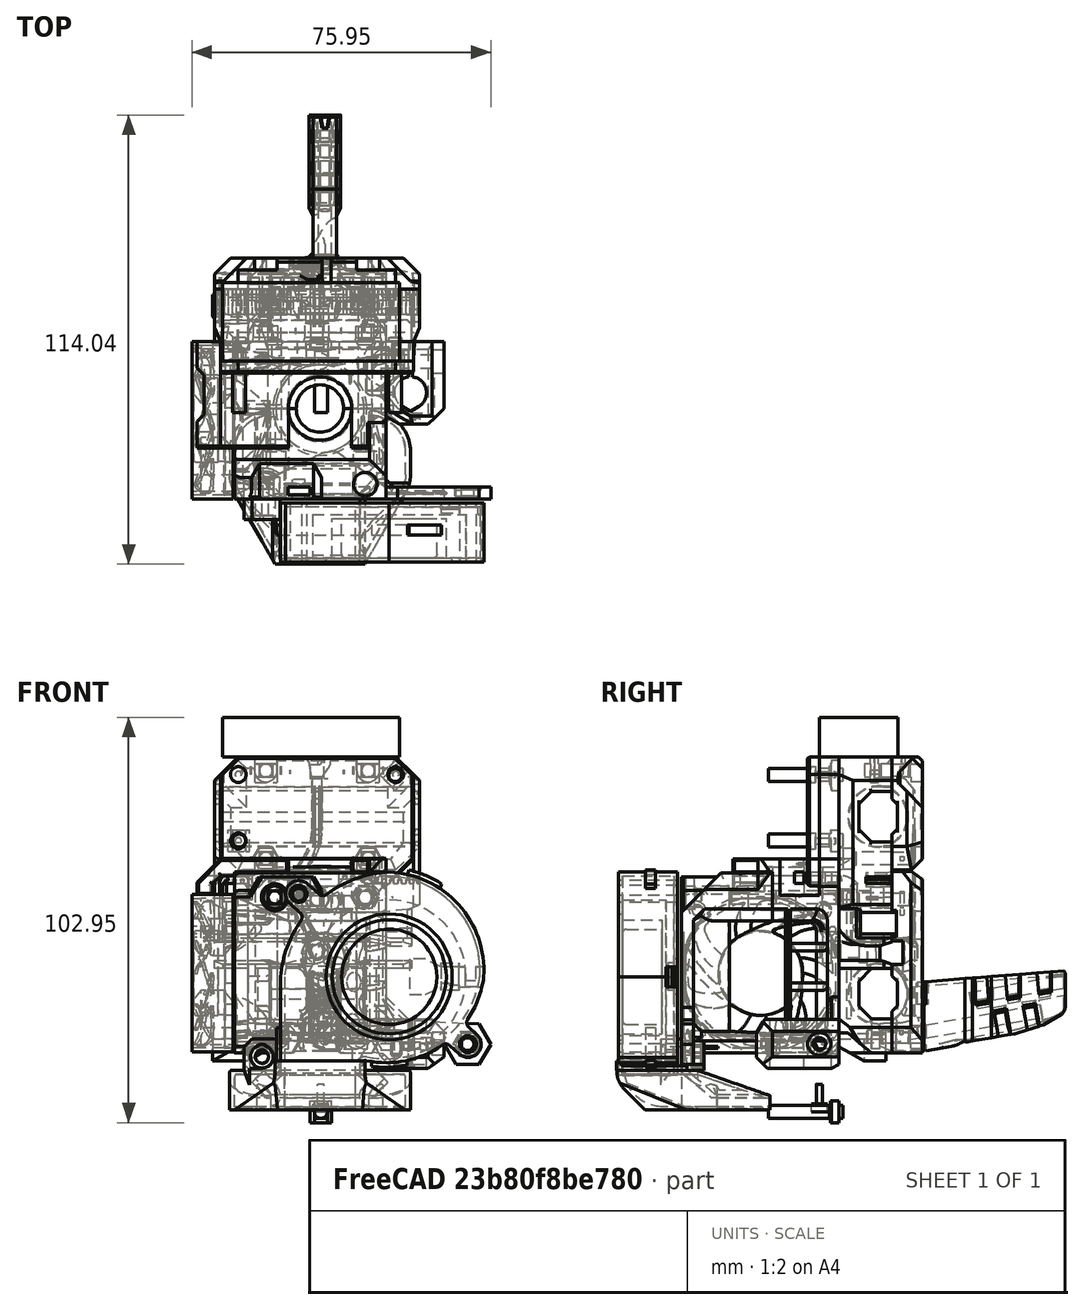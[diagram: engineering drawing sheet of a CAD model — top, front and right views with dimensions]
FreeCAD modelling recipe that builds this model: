
FCSTD DOCUMENT  (FreeCAD 0.18R16146 (Git))
Label: origin
License: All rights reserved
LicenseURL: http://en.wikipedia.org/wiki/All_rights_reserved
objects: Part::Feature×21, Part::Box×21, Part::Cut×14, Part::MultiFuse×7, Part::Chamfer×5, Part::Cylinder×3, Part::Fillet×1
note: 72 computed .brp shape members not serialized (recipe doc carries the construction recipe); baked Part::Feature solids carry a one-line shape summary decoded from their .brp

FEATURE [Part::Feature] Part__Feature005001  label="nozzle_fan_duct001"
  shape: bbox 46 x 38.98 x 18 mm, 128 faces (baked)
FEATURE [Part::Feature] Part__Feature006002  label="x_carriage_back_mk2.5s_v026"
  shape: bbox 52.01 x 8.271 x 75.21 mm, 515 faces, 2 solids (baked)
FEATURE [Part::Feature] Part__Feature003001  label="body001"
  shape: bbox 64.24 x 27.71 x 94.51 mm, 731 faces (baked)
FEATURE [Part::Feature] Part__Feature007001  label="cable_guide_back_a001"
  shape: bbox 9.081 x 19.43 x 18.86 mm, 61 faces (baked)
FEATURE [Part::Feature] Part__Feature008001  label="cable_guide_back_b001"
  shape: bbox 14.17 x 31.38 x 17 mm, 108 faces (baked)
FEATURE [Part::Feature] Part__Feature002001  label="cover001"
  shape: bbox 65.38 x 24.39 x 50.21 mm, 417 faces (baked)
FEATURE [Part::Feature] Part__Feature001001  label="x_carriage001"
  shape: bbox 52.5 x 22.36 x 91 mm, 735 faces (baked)
FEATURE [Part::Box] Box  label="Cube"
  AttacherType = Attacher::AttachEngine3D
  Height = 58
  Length = 78
  Placement = pos=(-37,-32,94) rot=(0,0,1;0rad)
  Width = 65
FEATURE [Part::Box] Box001  label="Cube001"
  AttacherType = Attacher::AttachEngine3D
  Height = 58
  Length = 78
  Placement = pos=(-37,-32,94) rot=(0,0,1;0rad)
  Width = 65
FEATURE [Part::Cut] Cut
  Base = -> Part__Feature001001
  Tool = -> Box001
FEATURE [Part::Cut] Cut001
  Base = -> Part__Feature003001
  Tool = -> Box
FEATURE [Part::Box] Box002  label="Cube002"
  AttacherType = Attacher::AttachEngine3D
  Height = 58
  Length = 78
  Placement = pos=(-37,-32,64.24) rot=(0,0,1;0rad)
  Width = 65
FEATURE [Part::Cut] Cut002
  Base = -> Cut001
  Tool = -> Box002
FEATURE [Part::Box] Box003  label="Cube003"
  AttacherType = Attacher::AttachEngine3D
  Height = 10
  Length = 16.06
  Placement = pos=(-8.26,-22,58) rot=(0,0,1;0rad)
  Width = 19
FEATURE [Part::Feature] Part__Feature046  label="nozzle_fan"
  Placement = pos=(-10.225,-36,34.3) rot=(0,0,1;1.5708rad)
  shape: bbox 52.65 x 15 x 52.12 mm, 76 faces (baked)
FEATURE [Part::Feature] Part__Feature008002  label="cover002"
  shape: bbox 65.38 x 24.39 x 50.21 mm, 417 faces (baked)
FEATURE [Part::Fillet] Fillet
  Base = -> Box003
  Edges = 2 edges r=8: [Edge3,Edge7]
  Placement = pos=(0,-1,0) rot=(0,0,1;0rad)
FEATURE [Part::Cut] Cut003
  Base = -> Cut002
  Tool = -> Fillet
FEATURE [Part::Box] Box004  label="Cube004"
  AttacherType = Attacher::AttachEngine3D
  Height = 1
  Length = 3
  Placement = pos=(6,-6,63.24) rot=(0,0,1;0rad)
  Width = 6
FEATURE [Part::Box] Box005  label="Cube005"
  AttacherType = Attacher::AttachEngine3D
  Height = 2
  Length = 36
  Placement = pos=(-22,-1,62.24) rot=(0,0,1;0rad)
  Width = 6
FEATURE [Part::Box] Box006  label="Cube006"
  AttacherType = Attacher::AttachEngine3D
  Height = 6
  Length = 6
  Placement = pos=(12.32,-24,59.24) rot=(0,0,1;0rad)
  Width = 8.43
FEATURE [Part::Cut] Cut004
  Base = -> Cut003
  Tool = -> Box006
FEATURE [Part::MultiFuse] Fusion
  Shapes = -> [Cut004,Box005,Box004]
FEATURE [Part::Box] Box007  label="Cube007"
  AttacherType = Attacher::AttachEngine3D
  Height = 17
  Length = 17
  Placement = pos=(-35.45,0,90.2) rot=(0,0,1;0rad)
  Width = 21
FEATURE [Part::Box] Box008  label="Cube008"
  AttacherType = Attacher::AttachEngine3D
  Height = 17
  Length = 17
  Placement = pos=(-37.97,0,84.2) rot=(0,0,1;0rad)
  Width = 21
FEATURE [Part::Cut] Cut005
  Base = -> Cut
  Tool = -> Box007
FEATURE [Part::Chamfer] Chamfer
  Base = -> Box008
  Edges = 1 edges r=6: [Edge8]
FEATURE [Part::Cut] Cut006
  Base = -> Cut005
  Tool = -> Chamfer
FEATURE [Part::Box] Box009  label="Cube009"
  AttacherType = Attacher::AttachEngine3D
  Height = 10
  Length = 45
  Placement = pos=(-25,0,90.2) rot=(0,0,1;0rad)
  Width = 20
FEATURE [Part::Box] Box010  label="Cube010"
  AttacherType = Attacher::AttachEngine3D
  Height = 10
  Length = 45
  Placement = pos=(-25,0,90.2) rot=(0,0,1;0rad)
  Width = 20
FEATURE [Part::Cut] Cut007  label="carrier-trim"
  Base = -> Cut006
  Tool = -> Box010
FEATURE [Part::Box] Box011  label="Cube011"
  AttacherType = Attacher::AttachEngine3D
  Height = 25.96
  Length = 49
  Placement = pos=(-25.48,0,64.24) rot=(0,0,1;0rad)
  Width = 5
FEATURE [Part::Box] Box012  label="Cube012"
  AttacherType = Attacher::AttachEngine3D
  Height = 7.96
  Length = 8
  Placement = pos=(15.52,0,57.24) rot=(0,0,1;0rad)
  Width = 5
FEATURE [Part::Chamfer] Chamfer001
  Base = -> Box012
  Edges = 1 edges r=7: [Edge8]
FEATURE [Part::Chamfer] Chamfer002
  Base = -> Box011
  Edges = 2 edges r=4.5: [Edge2,Edge6]
FEATURE [Part::MultiFuse] Fusion001
  Shapes = -> [Chamfer002,Chamfer001]
FEATURE [Part::Feature] Fusion001001  label="Fusion002"
  shape: bbox 49 x 5 x 32.96 mm, 11 faces (baked)
FEATURE [Part::Feature] Fusion001002  label="Fusion003"
  shape: bbox 49 x 5 x 32.96 mm, 11 faces (baked)
FEATURE [Part::Box] Box013  label="Cube013"
  AttacherType = Attacher::AttachEngine3D
  Height = 10
  Length = 50
  Placement = pos=(-33.38,0,54.34) rot=(0,0,1;0rad)
  Width = 10
FEATURE [Part::Cut] Cut008
  Base = -> Fusion001002
  Placement = pos=(0,-5,0) rot=(0,0,1;0rad)
  Tool = -> Box013
FEATURE [Part::MultiFuse] Fusion001003
  Shapes = -> [Fusion001,Fusion]
FEATURE [Part::Box] Box014  label="Cube014"
  AttacherType = Attacher::AttachEngine3D
  Height = 5.5
  Length = 1.1
  Placement = pos=(-2.75,-2.4,-2.75) rot=(0,0,1;0rad)
  Width = 0.4
FEATURE [Part::Cylinder] Cylinder
  Angle = 360
  AttacherType = Attacher::AttachEngine3D
  Height = 19
  Placement = pos=(0,1,-2e-16) rot=(1,0,0;1.5708rad)
  Radius = 1.65
FEATURE [Part::Box] Box015  label="Cube015"
  AttacherType = Attacher::AttachEngine3D
  Height = 1.1
  Length = 5.5
  Placement = pos=(-2.75,-2.4,-2.75) rot=(0,0,1;0rad)
  Width = 0.2
FEATURE [Part::Box] Box016  label="Cube016"
  AttacherType = Attacher::AttachEngine3D
  Height = 1.1
  Length = 5.5
  Placement = pos=(-2.75,-2.4,1.65) rot=(0,0,1;0rad)
  Width = 0.2
FEATURE [Part::Box] Box017  label="Cube017"
  AttacherType = Attacher::AttachEngine3D
  Height = 5.5
  Length = 5.5
  Placement = pos=(-2.75,-2.4,-2.75) rot=(0,0,1;0rad)
  Width = 2.4
FEATURE [Part::Box] Box018  label="Cube018"
  AttacherType = Attacher::AttachEngine3D
  Height = 5.5
  Length = 1.1
  Placement = pos=(1.65,-2.4,-2.75) rot=(0,0,1;0rad)
  Width = 0.4
FEATURE [Part::MultiFuse] Fusion001004
  Shapes = -> [Box015,Box016,Box018,Box014]
FEATURE [Part::Cut] Cut009
  Base = -> Box017
  Tool = -> Fusion001004
FEATURE [Part::MultiFuse] Fusion001005  label="bolt"
  Placement = pos=(0,5,0) rot=(0,0,1;0rad)
  Shapes = -> [Cut009,Cylinder]
FEATURE [Part::Feature] Fusion001005003002  label="bolt-set002"
  shape: bbox 46.34 x 19 x 23.29 mm, 42 faces, 2 solids (baked)
FEATURE [Part::Box] Box019  label="Cube019"
  AttacherType = Attacher::AttachEngine3D
  Height = 10
  Length = 10
  Placement = pos=(16.52,-10,55) rot=(0,0,1;0rad)
  Width = 10
FEATURE [Part::Box] Box020  label="Cube020"
  AttacherType = Attacher::AttachEngine3D
  Height = 35
  Length = 58
  Placement = pos=(-29,-13,56) rot=(0,0,1;0rad)
  Width = 10
FEATURE [Part::Feature] Part__Feature008003  label="nozzle_fan001"
  Placement = pos=(-10.225,-36,34.3) rot=(0,0,1;1.5708rad)
  shape: bbox 52.65 x 15 x 52.12 mm, 76 faces (baked)
FEATURE [Part::Feature] Part__Feature033  label="sunon_mf4010 v4"
  Placement = pos=(-22.275,5,15.25) rot=(0.707107,0,0.707107;3.14159rad)
  shape: bbox 10.74 x 40.01 x 40.01 mm, 116 faces (baked)
FEATURE [Part::Cut] Cut010002003
  Base = -> Cut008
  Tool = -> Box020
FEATURE [Part::Cut] Cut010002004
  Base = -> Fusion001003
  Tool = -> Box019
FEATURE [Part::Cylinder] Cylinder001
  Angle = 360
  AttacherType = Attacher::AttachEngine3D
  Height = 2
  Radius = 2
FEATURE [Part::Cylinder] Cylinder002
  Angle = 360
  AttacherType = Attacher::AttachEngine3D
  Height = 7
  Radius = 0.8
FEATURE [Part::MultiFuse] Fusion001005003003  label="m2-bolt"
  Shapes = -> [Cylinder002,Cylinder001]
FEATURE [Part::Feature] Fusion001005003003001  label="m2-bolt001"
  Placement = pos=(-20.98,-3,85.7) rot=(-1,0,0;1.5708rad)
  shape: bbox 4 x 7 x 4 mm, 5 faces (baked)
FEATURE [Part::Feature] Fusion001005003003002  label="m2-bolt002"
  Placement = pos=(-20.98,-3,68.84) rot=(-1,0,0;1.5708rad)
  shape: bbox 4 x 7 x 4 mm, 5 faces (baked)
FEATURE [Part::Feature] Fusion001005003003003  label="m2-bolt003"
  Placement = pos=(19.02,-3,85.7) rot=(-1,0,0;1.5708rad)
  shape: bbox 4 x 7 x 4 mm, 5 faces (baked)
FEATURE [Part::MultiFuse] Fusion001005003003004  label="front-bolt-set"
  Shapes = -> [Fusion001005003003003,Fusion001005003003001,Fusion001005003003002]
FEATURE [Part::Feature] Fusion001005003003004001  label="front-bolt-set001"
  shape: bbox 44 x 7 x 20.86 mm, 15 faces, 3 solids (baked)
FEATURE [Part::Feature] Fusion001005003003004002  label="front-bolt-set002"
  shape: bbox 44 x 7 x 20.86 mm, 15 faces, 3 solids (baked)
FEATURE [Part::Cut] Cut010002005
  Base = -> Cut010002003
  Tool = -> Fusion001005003003004001
FEATURE [Part::Cut] Cut010002006
  Base = -> Cut010002004
  Tool = -> Fusion001005003003004002
FEATURE [Part::Chamfer] Chamfer003
  Base = -> Cut010002005
  Edges = 6 edges r=0.4: [Edge1,Edge7,Edge8,Edge9,Edge10,Edge11]
FEATURE [Part::Feature] Cut010002006001  label="Cut010002007"
  shape: bbox 64.24 x 27.71 x 79.21 mm, 405 faces (baked)
FEATURE [Part::Chamfer] Chamfer004
  Base = -> Cut010002006001
  Edges = 8 edges r=0.4: [Edge134,Edge138,Edge139,Edge140,Edge184,Edge185,Edge187,Edge188]
FEATURE [Part::Feature] Cut007001  label="carrier-trim001"
  shape: bbox 52.5 x 22.36 x 77.2 mm, 678 faces (baked)
